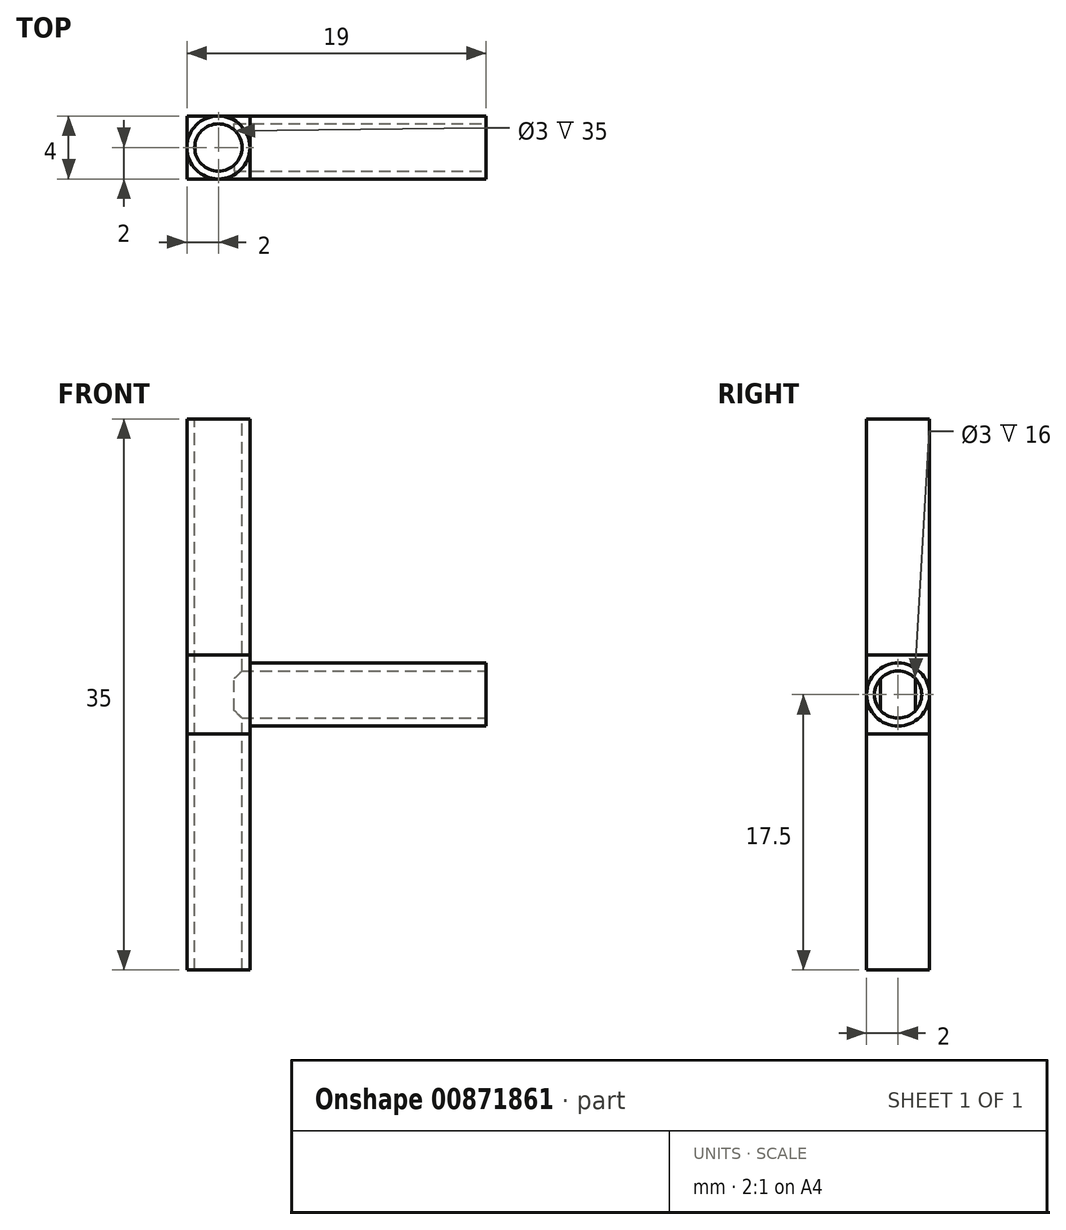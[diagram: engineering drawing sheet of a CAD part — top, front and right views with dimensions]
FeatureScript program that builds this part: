
annotation { "Feature Type Name" : "Feature", "Feature Type Description" : "" }
export const myFeature = defineFeature(function(context is Context, id is Id, definition is map)
    precondition{}
    {
        {
            assignVariable(context, id + "F0", {"name" : "Dlugosc_krocca", "anyValue" : 15});
        }
        {
            var Q0;
            Q0=qCreatedBy(makeId("Top.planeOp"),FACE);
            var sketch = newSketch(context, id + "F1", { "sketchPlane" : qUnion([Q0])});
            skLineSegment(sketch, "E0.bottom", {"start": v(2, -2) * mm, "end": v(-2, -2) * mm});
            skLineSegment(sketch, "E0.top", {"start": v(2, 2) * mm, "end": v(-2, 2) * mm});
            skLineSegment(sketch, "E0.left", {"start": v(2, -2) * mm, "end": v(2, 2) * mm});
            skLineSegment(sketch, "E0.right", {"start": v(-2, -2) * mm, "end": v(-2, 2) * mm});
            skPoint(sketch, "E0.middle", {"position": v(0, 0) * mm});
            skSolve(sketch);
        }
        {
            var Q0;
            Q0 = qSketchRegion(id + "F1", true);
            extrude(context, id + "F2", {"entities" : qUnion([Q0]), "endBound" : BoundingType.SYMMETRIC, "depth" : 5 * mm, "offsetDistance" : 25 * mm});
        }
        {
            var Q0;
            Q0=makeQuery(id+"F2.opExtrude","CAP_FACE",FACE,{"disambiguationData":[OSD([sQuery(id+"F1.wireOp",EDGE,"E0.bottom"),sQuery(id+"F1.wireOp",EDGE,"E0.top"),sQuery(id+"F1.wireOp",EDGE,"E0.left"),sQuery(id+"F1.wireOp",EDGE,"E0.right")])],"isStart":false});
            var sketch = newSketch(context, id + "F3", { "sketchPlane" : qUnion([Q0])});
            skCircle(sketch, "E1", {"center": v(0, 0) * mm, "radius": 2 * mm});
            skSolve(sketch);
        }
        {
            var Q0;
            Q0 = qSketchRegion(id + "F3", true);
            extrude(context, id + "F4", {"entities" : qUnion([Q0]), "operationType" : NewBodyOperationType.ADD, "depth" : (getVariable(context, 'Dlugosc_krocca')) * mm, "offsetDistance" : 25 * mm});
        }
        {
            var Q0;
            Q0=makeQuery(id+"F2.opExtrude","CAP_FACE",FACE,{"disambiguationData":[OSD([sQuery(id+"F1.wireOp",EDGE,"E0.bottom"),sQuery(id+"F1.wireOp",EDGE,"E0.top"),sQuery(id+"F1.wireOp",EDGE,"E0.left"),sQuery(id+"F1.wireOp",EDGE,"E0.right")])],"isStart":true});
            var sketch = newSketch(context, id + "F5", { "sketchPlane" : qUnion([Q0])});
            skCircle(sketch, "E2", {"center": v(0, 0) * mm, "radius": 2 * mm});
            skSolve(sketch);
        }
        {
            var Q0;
            Q0 = qSketchRegion(id + "F5", true);
            extrude(context, id + "F6", {"entities" : qUnion([Q0]), "operationType" : NewBodyOperationType.ADD, "depth" : (getVariable(context, 'Dlugosc_krocca')) * mm, "offsetDistance" : 25 * mm});
        }
        {
            var Q0;
            Q0=makeQuery(id+"F2.opExtrude","SWEPT_FACE",FACE,{"disambiguationData":[OSD([sQuery(id+"F1.wireOp",EDGE,"E0.left")])]});
            var sketch = newSketch(context, id + "F7", { "sketchPlane" : qUnion([Q0])});
            skCircle(sketch, "E3", {"center": v(0, 0) * mm, "radius": 2 * mm});
            skSolve(sketch);
        }
        {
            var Q0;
            Q0 = qSketchRegion(id + "F7", true);
            extrude(context, id + "F8", {"entities" : qUnion([Q0]), "operationType" : NewBodyOperationType.ADD, "depth" : (getVariable(context, 'Dlugosc_krocca')) * mm, "offsetDistance" : 25 * mm});
        }
        {
            var Q0;
            Q0=makeQuery(id+"F4.opExtrude","CAP_FACE",FACE,{"disambiguationData":[OSD([sQuery(id+"F3.wireOp",EDGE,"E1")])],"isStart":false});
            var sketch = newSketch(context, id + "F9", { "sketchPlane" : qUnion([Q0])});
            skCircle(sketch, "E4", {"center": v(0, 0) * mm, "radius": 1.5 * mm});
            skSolve(sketch);
        }
        {
            var Q0;
            Q0 = qSketchRegion(id + "F9", true);
            extrude(context, id + "F10", {"entities" : qUnion([Q0]), "operationType" : NewBodyOperationType.REMOVE, "endBound" : BoundingType.THROUGH_ALL, "oppositeDirection" : true, "depth" : 25 * mm, "offsetDistance" : 25 * mm});
        }
        {
            var Q0;
            Q0=makeQuery(id+"F8.opExtrude","CAP_FACE",FACE,{"disambiguationData":[OSD([sQuery(id+"F7.wireOp",EDGE,"E3")])],"isStart":false});
            var sketch = newSketch(context, id + "F11", { "sketchPlane" : qUnion([Q0])});
            skCircle(sketch, "E5", {"center": v(0, 0) * mm, "radius": 1.5 * mm});
            skSolve(sketch);
        }
        {
            var Q0;
            Q0 = qSketchRegion(id + "F11", true);
            extrude(context, id + "F12", {"entities" : qUnion([Q0]), "operationType" : NewBodyOperationType.REMOVE, "oppositeDirection" : true, "depth" : ((getVariable(context, 'Dlugosc_krocca')) + 1) * mm, "offsetDistance" : 25 * mm});
        }
    });
